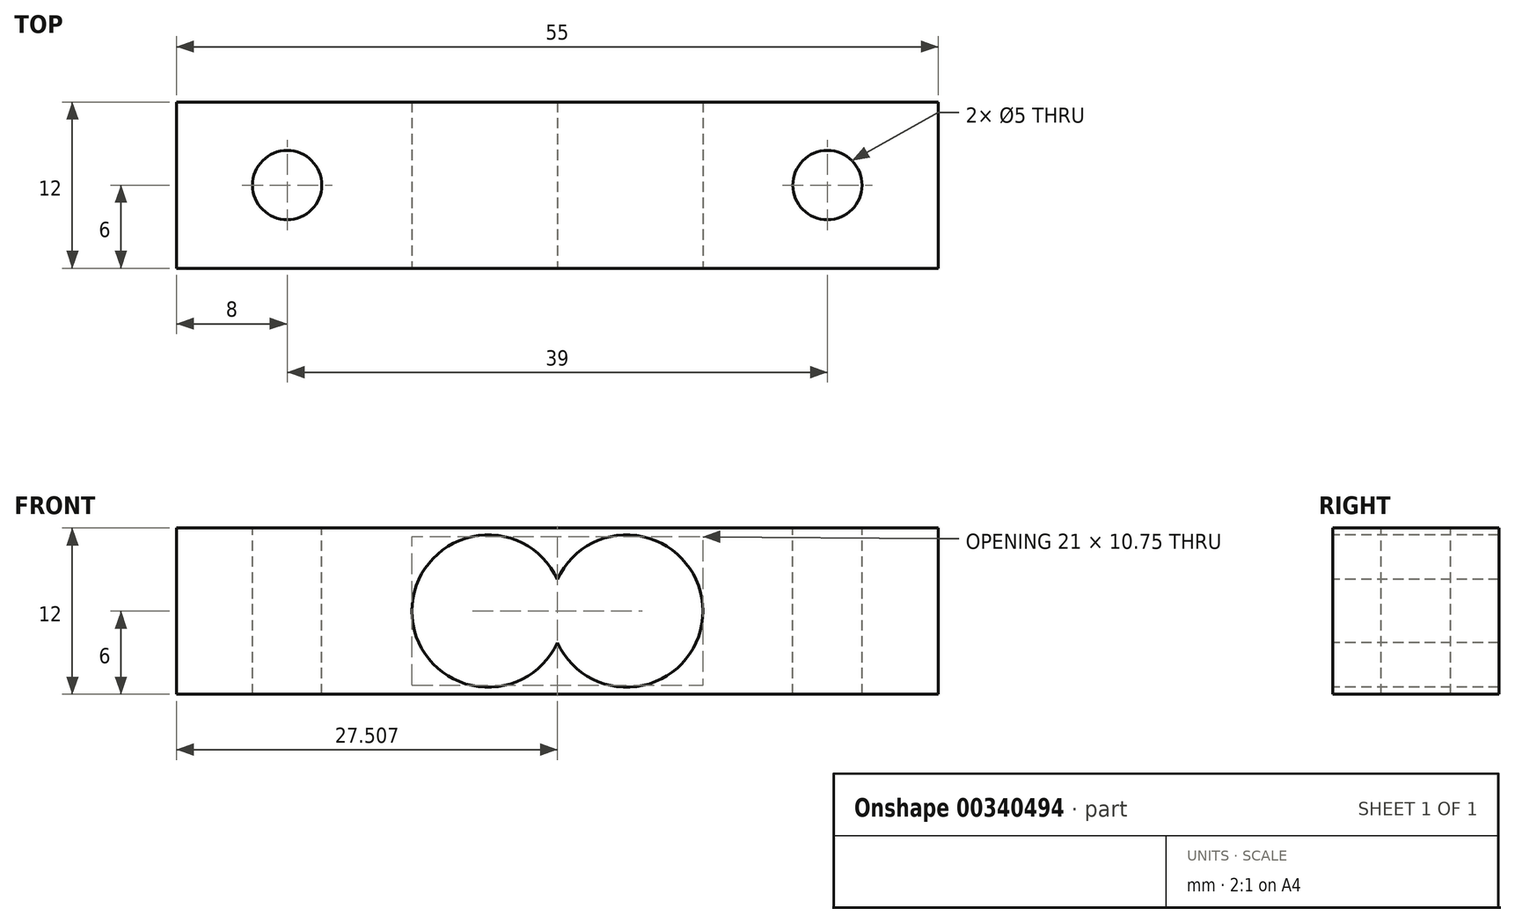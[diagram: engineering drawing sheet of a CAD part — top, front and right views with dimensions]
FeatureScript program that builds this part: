
annotation { "Feature Type Name" : "Feature", "Feature Type Description" : "" }
export const myFeature = defineFeature(function(context is Context, id is Id, definition is map)
    precondition{}
    {
        {
            var Q0;
            Q0=qCreatedBy(makeId("Top.planeOp"),FACE);
            var sketch = newSketch(context, id + "F0", { "sketchPlane" : qUnion([Q0])});
            skLineSegment(sketch, "E0.bottom", {"start": v(27.5, -6) * mm, "end": v(-27.5, -6) * mm});
            skLineSegment(sketch, "E0.top", {"start": v(27.5, 6) * mm, "end": v(-27.5, 6) * mm});
            skLineSegment(sketch, "E0.left", {"start": v(27.5, -6) * mm, "end": v(27.5, 6) * mm});
            skLineSegment(sketch, "E0.right", {"start": v(-27.5, -6) * mm, "end": v(-27.5, 6) * mm});
            skPoint(sketch, "E0.middle", {"position": v(0, 0) * mm});
            skSolve(sketch);
        }
        {
            var Q0;
            Q0=qSketchRegion(id+"F0",true);
            extrude(context, id + "F1", {"entities" : qUnion([Q0]), "endBound" : BoundingType.SYMMETRIC, "depth" : 12 * mm});
        }
        {
            var Q0;
            Q0=makeQuery(id+"F1.opExtrude","CAP_FACE",FACE,{"disambiguationData":[OSD([sQuery(id+"F0.wireOp",EDGE,"E0.bottom"),sQuery(id+"F0.wireOp",EDGE,"E0.top"),sQuery(id+"F0.wireOp",EDGE,"E0.left"),sQuery(id+"F0.wireOp",EDGE,"E0.right")])],"isStart":false});
            var sketch = newSketch(context, id + "F2", { "sketchPlane" : qUnion([Q0])});
            skCircle(sketch, "E1", {"center": v(-19.5, 0) * mm, "radius": 2.5 * mm});
            skCircle(sketch, "E2", {"center": v(19.5, 0) * mm, "radius": 2.5 * mm});
            skSolve(sketch);
        }
        {
            var Q0;
            Q0=makeQuery(id+"F2.imprint","IMPRINT",FACE,{"disambiguationData":[TD([[makeQuery(id+"F2.imprint","IMPRINT",EDGE,{"derivedFrom":sQuery(id+"F2.wireOp",EDGE,"E1")}),1.0]])]});
            var Q1;
            Q1=makeQuery(id+"F2.imprint","IMPRINT",FACE,{"disambiguationData":[TD([[makeQuery(id+"F2.imprint","IMPRINT",EDGE,{"derivedFrom":sQuery(id+"F2.wireOp",EDGE,"E2")}),1.0]])]});
            extrude(context, id + "F3", {"entities" : qUnion([Q0, Q1]), "operationType" : NewBodyOperationType.REMOVE, "endBound" : BoundingType.THROUGH_ALL, "oppositeDirection" : true, "depth" : 25 * mm});
        }
        {
            var Q0;
            Q0=makeQuery(id+"F1.opExtrude","SWEPT_FACE",FACE,{"disambiguationData":[OSD([sQuery(id+"F0.wireOp",EDGE,"E0.bottom")])]});
            var sketch = newSketch(context, id + "F4", { "sketchPlane" : qUnion([Q0])});
            skArc(sketch, "E3", {"start": v(0, -2.3) * mm, "mid": v(10.5, 0) * mm, "end": v(0, 2.3) * mm});
            skArc(sketch, "E4", {"start": v(0, 2.3) * mm, "mid": v(-10.5, 0) * mm, "end": v(0, -2.3) * mm});
            skSolve(sketch);
        }
        {
            var Q0;
            Q0=qSketchRegion(id+"F4",true);
            extrude(context, id + "F5", {"entities" : qUnion([Q0]), "operationType" : NewBodyOperationType.REMOVE, "oppositeDirection" : true, "depth" : 25 * mm});
        }
    });
